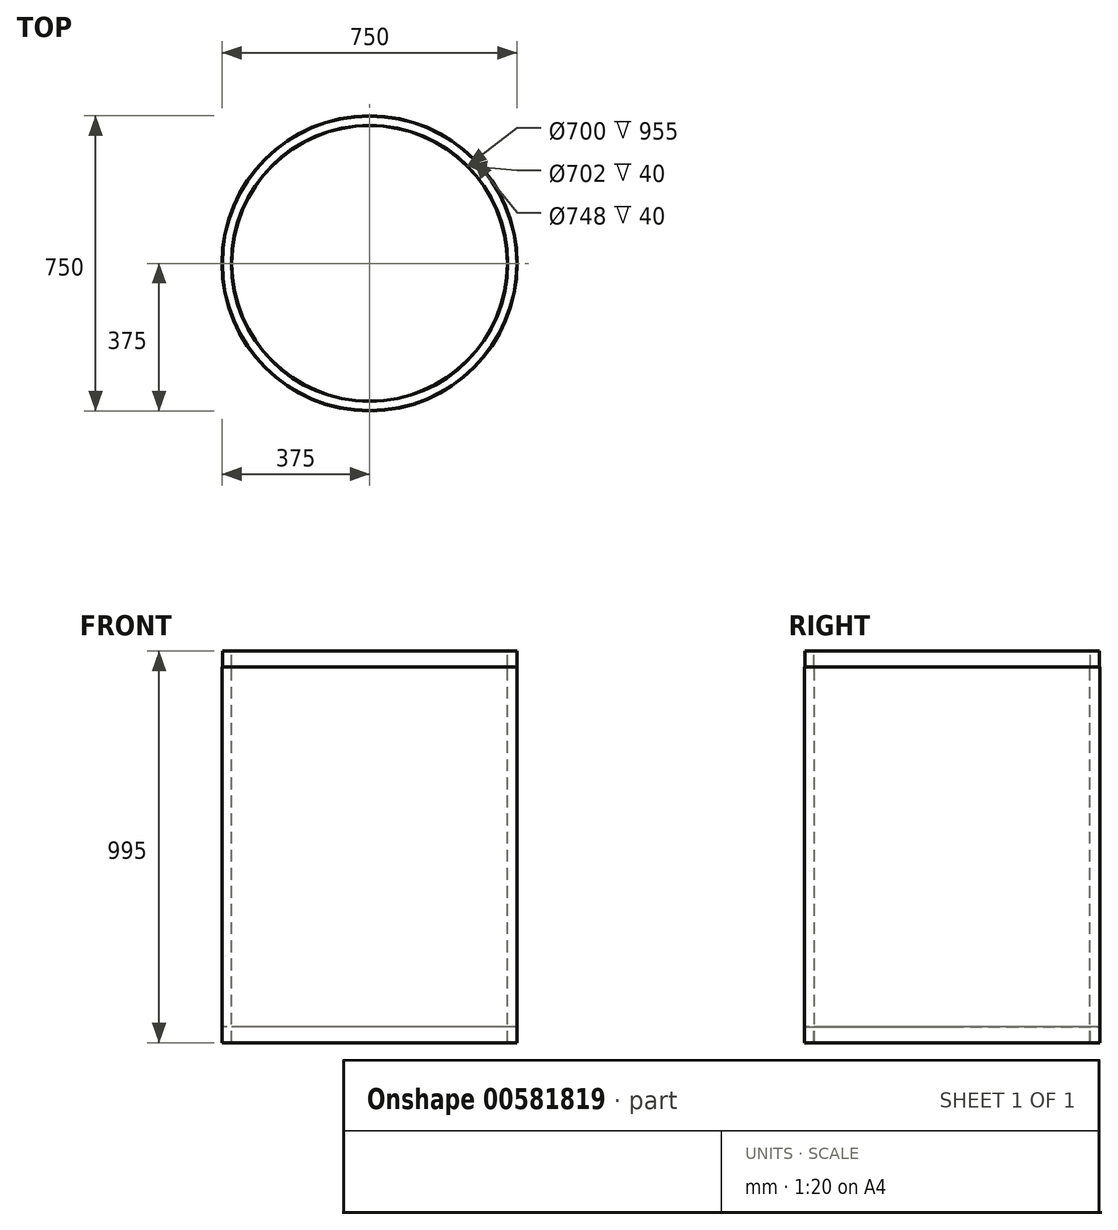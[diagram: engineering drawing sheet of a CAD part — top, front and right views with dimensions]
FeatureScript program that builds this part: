
annotation { "Feature Type Name" : "Feature", "Feature Type Description" : "" }
export const myFeature = defineFeature(function(context is Context, id is Id, definition is map)
    precondition{}
    {
        {
            var Q0;
            Q0=qCreatedBy(makeId("Front.planeOp"),FACE);
            var sketch = newSketch(context, id + "F0", { "sketchPlane" : qUnion([Q0])});
            skLineSegment(sketch, "E0", {"start": v(0, 345.75) * mm, "end": v(0, -558.03) * mm, "construction": true});
            skLineSegment(sketch, "E1", {"start": v(-350, -518.84) * mm, "end": v(-350, 436.16) * mm});
            skLineSegment(sketch, "E2", {"start": v(-350, 436.16) * mm, "end": v(-351, 436.16) * mm});
            skLineSegment(sketch, "E3", {"start": v(-351, 436.16) * mm, "end": v(-351, 476.16) * mm});
            skLineSegment(sketch, "E4", {"start": v(-351, 476.16) * mm, "end": v(-374, 476.16) * mm});
            skLineSegment(sketch, "E5", {"start": v(-374, 476.16) * mm, "end": v(-374, 436.16) * mm});
            skLineSegment(sketch, "E6", {"start": v(-374, 436.16) * mm, "end": v(-375, 436.16) * mm});
            skLineSegment(sketch, "E7", {"start": v(-375, 436.16) * mm, "end": v(-375, -518.84) * mm});
            skLineSegment(sketch, "E8", {"start": v(-375, -518.84) * mm, "end": v(-374, -518.84) * mm});
            skLineSegment(sketch, "E9", {"start": v(-374, -518.84) * mm, "end": v(-374, -478.84) * mm});
            skLineSegment(sketch, "E10", {"start": v(-374, -478.84) * mm, "end": v(-351, -478.84) * mm});
            skLineSegment(sketch, "E11", {"start": v(-351, -478.84) * mm, "end": v(-351, -518.84) * mm});
            skLineSegment(sketch, "E12", {"start": v(-351, -518.84) * mm, "end": v(-350, -518.84) * mm});
            skSolve(sketch);
        }
        {
            var Q0;
            Q0 = qSketchRegion(id + "F0", true);
            var Q1;
            Q1=sQuery(id+"F0.wireOp",EDGE,"E0");
            revolve(context, id + "F1", {"entities" : qUnion([Q0]), "axis" : qUnion([Q1]), "revolveType" : RevolveType.FULL});
        }
    });
